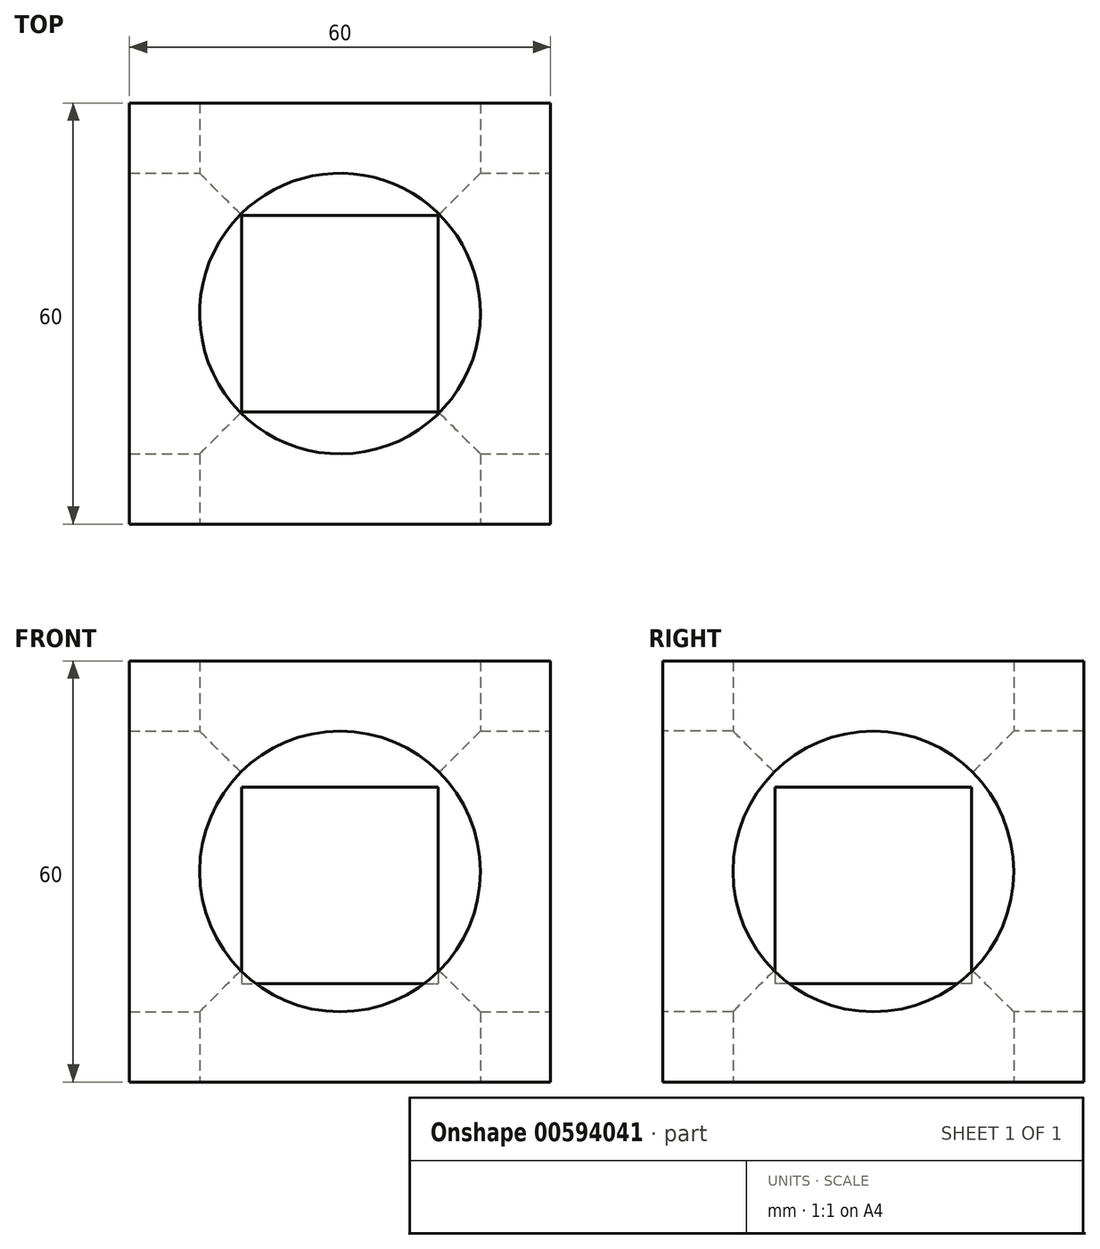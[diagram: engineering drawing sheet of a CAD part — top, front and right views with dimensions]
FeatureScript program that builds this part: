
annotation { "Feature Type Name" : "Feature", "Feature Type Description" : "" }
export const myFeature = defineFeature(function(context is Context, id is Id, definition is map)
    precondition{}
    {
        {
            var Q0;
            Q0=qCreatedBy(makeId("Top.planeOp"),FACE);
            var sketch = newSketch(context, id + "F0", { "sketchPlane" : qUnion([Q0])});
            skLineSegment(sketch, "E0.bottom", {"start": v(-30, 30) * mm, "end": v(30, 30) * mm});
            skLineSegment(sketch, "E0.top", {"start": v(-30, -30) * mm, "end": v(30, -30) * mm});
            skLineSegment(sketch, "E0.left", {"start": v(-30, 30) * mm, "end": v(-30, -30) * mm});
            skLineSegment(sketch, "E0.right", {"start": v(30, 30) * mm, "end": v(30, -30) * mm});
            skPoint(sketch, "E0.middle", {"position": v(0, 0) * mm});
            skLineSegment(sketch, "E1.bottom", {"start": v(-14, 14) * mm, "end": v(14, 14) * mm});
            skLineSegment(sketch, "E1.top", {"start": v(-14, -14) * mm, "end": v(14, -14) * mm});
            skLineSegment(sketch, "E1.left", {"start": v(-14, 14) * mm, "end": v(-14, -14) * mm});
            skLineSegment(sketch, "E1.right", {"start": v(14, 14) * mm, "end": v(14, -14) * mm});
            skCircle(sketch, "E2", {"center": v(0, 0) * mm, "radius": 20 * mm});
            skSolve(sketch);
        }
        {
            var Q0;
            Q0=makeQuery(id+"F0.imprint","IMPRINT",FACE,{"disambiguationData":[TD([[makeQuery(id+"F0.imprint","IMPRINT",EDGE,{"derivedFrom":sQuery(id+"F0.wireOp",EDGE,"E0.bottom")}),-1.0]])]});
            extrude(context, id + "F1", {"entities" : qUnion([Q0]), "depth" : 60 * mm, "offsetDistance" : 25 * mm});
        }
        {
            var Q0;
            Q0=qCreatedBy(makeId("Right.planeOp"),FACE);
            var sketch = newSketch(context, id + "F2", { "sketchPlane" : qUnion([Q0])});
            skCircle(sketch, "E3", {"center": v(0, 30) * mm, "radius": 20 * mm});
            skSolve(sketch);
        }
        {
            var Q0;
            Q0=makeQuery(id+"F2.imprint","IMPRINT",FACE,{"disambiguationData":[TD([[makeQuery(id+"F2.imprint","IMPRINT",EDGE,{"derivedFrom":sQuery(id+"F2.wireOp",EDGE,"E3")}),1.0]])]});
            extrude(context, id + "F3", {"entities" : qUnion([Q0]), "operationType" : NewBodyOperationType.REMOVE, "endBound" : BoundingType.SYMMETRIC, "oppositeDirection" : true, "depth" : 60 * mm, "offsetDistance" : 25 * mm});
        }
        {
            var Q0;
            Q0=qCreatedBy(makeId("Front.planeOp"),FACE);
            var sketch = newSketch(context, id + "F4", { "sketchPlane" : qUnion([Q0])});
            skCircle(sketch, "E4", {"center": v(0, 30) * mm, "radius": 20 * mm});
            skSolve(sketch);
        }
        {
            var Q0;
            Q0=makeQuery(id+"F4.imprint","IMPRINT",FACE,{"disambiguationData":[TD([[makeQuery(id+"F4.imprint","IMPRINT",EDGE,{"derivedFrom":sQuery(id+"F4.wireOp",EDGE,"E4")}),1.0]])]});
            extrude(context, id + "F5", {"entities" : qUnion([Q0]), "operationType" : NewBodyOperationType.REMOVE, "endBound" : BoundingType.SYMMETRIC, "oppositeDirection" : true, "depth" : 60 * mm, "offsetDistance" : 25 * mm});
        }
        {
            var Q0;
            Q0=makeQuery(id+"F0.imprint","IMPRINT",FACE,{"disambiguationData":[TD([[makeQuery(id+"F0.imprint","IMPRINT",EDGE,{"derivedFrom":sQuery(id+"F0.wireOp",EDGE,"E1.bottom")}),-1.0]])]});
            extrude(context, id + "F6", {"entities" : qUnion([Q0]), "depth" : 42 * mm, "offsetDistance" : 25 * mm, "hasSecondDirection" : true, "secondDirectionOppositeDirection" : false, "secondDirectionDepth" : 14 * mm});
        }
    });
